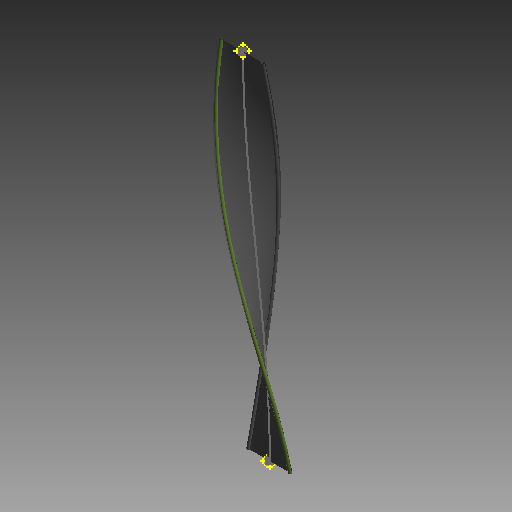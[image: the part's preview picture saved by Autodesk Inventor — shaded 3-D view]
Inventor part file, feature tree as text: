
AUTODESK INVENTOR PART (.ipt)
format: ipt  version: 2019 (Build 230136000, 136)  size: 140,800 bytes
history: native  units: mm (DEFAULTED — no unit token found)
features: other x6, sketch x3, sweep x3
ambient origin geometry x8: Origin, YZ Plane, XZ Plane, XY Plane, X Axis, Y Axis, Z Axis, Center Point
bodies: Body1 (feature_tree), Body2 (feature_tree), Body3 (feature_tree)
feature tree (12):
  other  "Work Point1"
  other  "Work Point2"
  other  "RibbonCable1"
  sketch  "Sketch1"  dims[d0=0.0mm d1=0.0mm d2=0.0mm d3=0.0mm]
  sketch  "Sketch2"  dims[d4=0.0mm d5=0.0mm]
  sketch  "Sketch3"
  other  "Srf1"
  other  "Srf2"
  other  "Srf3"
  sweep  "SweepSrf1"
  sweep  "SweepSrf2"
  sweep  "SweepSrf3"
